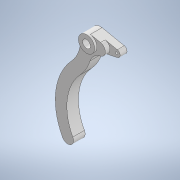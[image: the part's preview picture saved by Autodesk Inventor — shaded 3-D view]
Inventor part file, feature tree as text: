
AUTODESK INVENTOR PART (.ipt)
format: ipt  version: 2020 (Build 240168000, 168)  size: 173,568 bytes
history: native  units: mm
features: extrude x3, sketch x3, projected_geometry x2
ambient origin geometry x8: Origin, YZ Plane, XZ Plane, XY Plane, X Axis, Y Axis, Z Axis, Center Point
bodies: Solid1 (feature_tree)
feature tree (8):
  extrude  "Extrusion1"  Depth=5.0mm
  extrude  "Extrusion2"  Depth=1.0mm
  extrude  "Extrusion3"  Depth=3.0mm TaperAngle=0.0deg
  sketch  "Sketch1"  dims[d0=5.0mm d1=7.0mm]
  sketch  "Sketch2"  dims[d2=3.0mm d3=1.0mm]
  projected_geometry  "Projected Loop1"
  sketch  "Sketch3"  dims[d4=10.0mm d5=3.0mm d6=0.0mm d7=3.0mm d8=0.0mm d9=21.816616mm d10=24.0mm d11=42.0mm d12=12.0mm d13=62.0mm d14=42.0mm d17=15.0mm d18=26.5mm d19=5.0mm d20=5.0mm d21=6.0mm d22=40.0mm d23=5.0mm d24=0.0mm]
  projected_geometry  "Projected Loop2"
